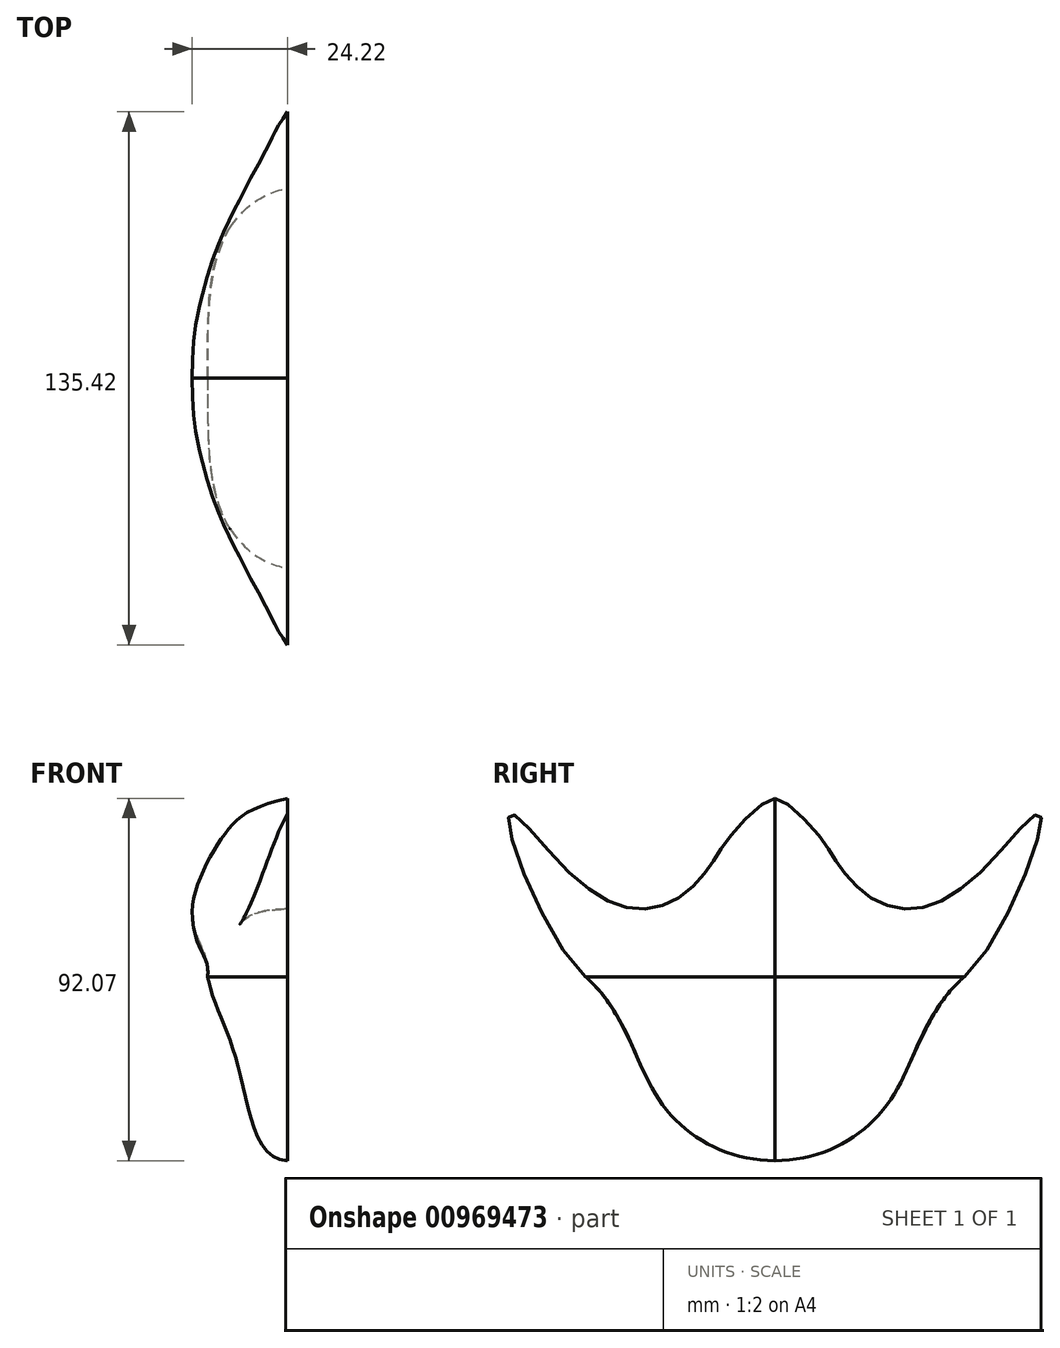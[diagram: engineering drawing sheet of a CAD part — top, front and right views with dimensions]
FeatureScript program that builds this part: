
annotation { "Feature Type Name" : "Feature", "Feature Type Description" : "" }
export const myFeature = defineFeature(function(context is Context, id is Id, definition is map)
    precondition{}
    {
        {
            var Q0;
            Q0=qCreatedBy(makeId("Top.planeOp"),FACE);
            var sketch = newSketch(context, id + "F0", { "sketchPlane" : qUnion([Q0])});
            skFitSpline(sketch, "E0.MirrorCS", {"points": [v(-20.27, 0) * mm, v(-15.56, -36.68) * mm, v(0, -48.13) * mm], "startDerivative": vector(0, -86.18) * mm, "endDerivative": vector(43.06, -4.03) * mm});
            skSolve(sketch);
        }
        {
            var Q0;
            Q0=qCreatedBy(makeId("Right.planeOp"),FACE);
            var sketch = newSketch(context, id + "F1", { "sketchPlane" : qUnion([Q0])});
            skFitSpline(sketch, "E1", {"points": [v(0, 45.34) * mm, v(-11.13, 35.98) * mm, v(-16.27, 28.36) * mm, v(-24.73, 19.87) * mm, v(-36.74, 17.47) * mm, v(-54.05, 28.36) * mm, v(-67.53, 41.13) * mm, v(-48.13, 0) * mm], "startDerivative": vector(-55.7, 0) * mm, "endDerivative": vector(130, -112.83) * mm});
            skFitSpline(sketch, "E2.MirrorCS", {"points": [v(0, -46.73) * mm, v(-28.9, -32) * mm, v(-48.13, 0) * mm], "startDerivative": vector(-74.6, 0) * mm, "endDerivative": vector(-63.4, 55.04) * mm});
            skSolve(sketch);
        }
        {
            var Q0;
            Q0=qCreatedBy(makeId("Front.planeOp"),FACE);
            var sketch = newSketch(context, id + "F2", { "sketchPlane" : qUnion([Q0])});
            skPoint(sketch, "E3.0", {"position": v(0, 45.34) * mm});
            skPoint(sketch, "E4.0", {"position": v(-20.27, 0) * mm});
            skFitSpline(sketch, "E5", {"points": [v(-20.27, 0) * mm, v(-24.15, 14.8) * mm, v(-17.28, 34.3) * mm, v(0, 45.34) * mm], "startDerivative": vector(6.17, 54.45) * mm, "endDerivative": vector(90.74, 20.13) * mm});
            skPoint(sketch, "E6.0", {"position": v(0, -46.73) * mm});
            skFitSpline(sketch, "E7", {"points": [v(-20.27, 0) * mm, v(-12.62, -22.32) * mm, v(0, -46.73) * mm], "startDerivative": vector(10.24, -49.63) * mm, "endDerivative": vector(49.8, 0) * mm});
            skSolve(sketch);
        }
        {
            var Q0;
            Q0=sQuery(id+"F0.wireOp",EDGE,"E0.MirrorCS");
            var Q1;
            Q1=sQuery(id+"F1.wireOp",EDGE,"E1");
            var Q2;
            Q2=sQuery(id+"F2.wireOp",EDGE,"E5");
            loft(context, id + "F3", {"bodyType" : ToolBodyType.SURFACE, "wireProfilesArray" : [{ "wireProfileEntities" : qUnion([Q0]) }, { "wireProfileEntities" : qUnion([Q1]) }], "addGuides" : true, "guidesArray" : [{ "guideEntities" : qUnion([Q2]), "guideDerivativeType" : LoftGuideDerivativeType.DEFAULT, "guideDerivativeMagnitude" : 1 }]});
        }
        {
            var Q0;
            Q0=sQuery(id+"F0.wireOp",EDGE,"E0.MirrorCS");
            var Q1;
            Q1=sQuery(id+"F1.wireOp",EDGE,"E2.MirrorCS");
            var Q2;
            Q2=sQuery(id+"F2.wireOp",EDGE,"E7");
            loft(context, id + "F4", {"bodyType" : ToolBodyType.SURFACE, "surfaceOperationType" : NewSurfaceOperationType.ADD, "wireProfilesArray" : [{ "wireProfileEntities" : qUnion([Q0]) }, { "wireProfileEntities" : qUnion([Q1]) }], "addGuides" : true, "guidesArray" : [{ "guideEntities" : qUnion([Q2]), "guideDerivativeType" : LoftGuideDerivativeType.DEFAULT, "guideDerivativeMagnitude" : 1 }]});
        }
        {
            var Q0;
            Q0=makeQuery(id+"F3.opLoft","SWEPT_BODY",BODY,{"disambiguationData":[OSD([sQuery(id+"F0.wireOp",EDGE,"E0.MirrorCS"),sQuery(id+"F1.wireOp",EDGE,"E1"),sQuery(id+"F2.wireOp",EDGE,"E5")])]});
            var Q1;
            Q1=qCreatedBy(makeId("Front.planeOp"),FACE);
            mirror(context, id + "F5", {"entities" : qUnion([Q0]), "mirrorPlane" : qUnion([Q1])});
        }
    });
